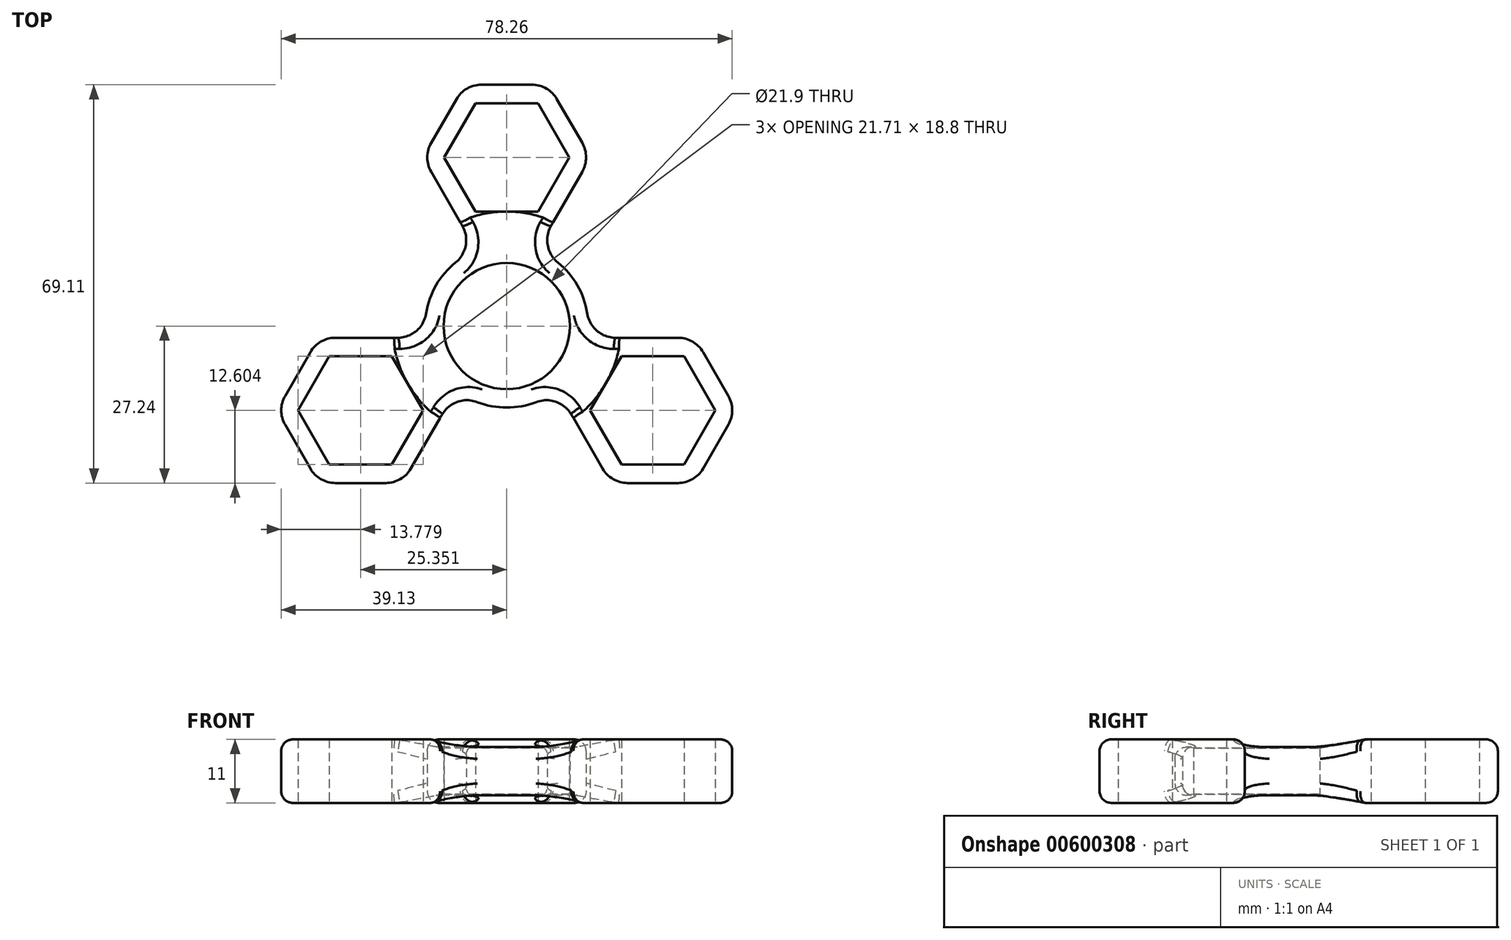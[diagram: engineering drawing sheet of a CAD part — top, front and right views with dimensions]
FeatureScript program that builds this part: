
annotation { "Feature Type Name" : "Feature", "Feature Type Description" : "" }
export const myFeature = defineFeature(function(context is Context, id is Id, definition is map)
    precondition{}
    {
        {
            var Q0;
            Q0=qCreatedBy(makeId("Top.planeOp"),FACE);
            var sketch = newSketch(context, id + "F0", { "sketchPlane" : qUnion([Q0])});
            skCircle(sketch, "E0", {"center": v(0, 0) * mm, "radius": 42.5 * mm, "construction": true});
            skLineSegment(sketch, "E1", {"start": v(0, 29.27) * mm, "end": v(0, 0) * mm, "construction": true});
            skLineSegment(sketch, "E2", {"start": v(0, 0) * mm, "end": v(-25.35, -14.64) * mm, "construction": true});
            skLineSegment(sketch, "E3", {"start": v(0, 0) * mm, "end": v(25.35, -14.64) * mm, "construction": true});
            skCircle(sketch, "E4.cCircle", {"center": v(0, 29.27) * mm, "radius": 9.4 * mm, "construction": true});
            skLineSegment(sketch, "E4.0", {"start": v(10.85, 29.27) * mm, "end": v(5.43, 19.87) * mm});
            skLineSegment(sketch, "E4.1", {"start": v(5.43, 19.87) * mm, "end": v(-5.43, 19.87) * mm});
            skLineSegment(sketch, "E4.2", {"start": v(-5.43, 19.87) * mm, "end": v(-10.85, 29.27) * mm});
            skLineSegment(sketch, "E4.3", {"start": v(-10.85, 29.27) * mm, "end": v(-5.43, 38.67) * mm});
            skLineSegment(sketch, "E4.4", {"start": v(-5.43, 38.67) * mm, "end": v(5.43, 38.67) * mm});
            skLineSegment(sketch, "E4.5", {"start": v(5.43, 38.67) * mm, "end": v(10.85, 29.27) * mm});
            skPoint(sketch, "E4.0.midPoint", {"position": v(8.14, 24.57) * mm});
            skCircle(sketch, "E5.cCircle", {"center": v(0, 29.27) * mm, "radius": 12.6 * mm, "construction": true});
            skLineSegment(sketch, "E5.0", {"start": v(14.55, 29.27) * mm, "end": v(7.27, 16.67) * mm});
            skLineSegment(sketch, "E5.1", {"start": v(7.27, 16.67) * mm, "end": v(0, 16.67) * mm});
            skLineSegment(sketch, "E5.2", {"start": v(-7.27, 16.67) * mm, "end": v(-14.55, 29.27) * mm});
            skLineSegment(sketch, "E5.3", {"start": v(-14.55, 29.27) * mm, "end": v(-7.27, 41.87) * mm});
            skLineSegment(sketch, "E5.4", {"start": v(-7.27, 41.87) * mm, "end": v(7.27, 41.87) * mm});
            skLineSegment(sketch, "E5.5", {"start": v(7.27, 41.87) * mm, "end": v(14.55, 29.27) * mm});
            skPoint(sketch, "E5.0.midPoint", {"position": v(10.91, 22.97) * mm});
            skLineSegment(sketch, "E6", {"start": v(-7.27, 16.67) * mm, "end": v(-5.24, 13.14) * mm});
            skLineSegment(sketch, "E7", {"start": v(7.27, 16.67) * mm, "end": v(5.24, 13.14) * mm});
            skCircle(sketch, "E8", {"center": v(0, 0) * mm, "radius": 10.95 * mm});
            skCircle(sketch, "E9.cCircle", {"center": v(25.35, -14.64) * mm, "radius": 9.4 * mm, "construction": true});
            skLineSegment(sketch, "E9.0", {"start": v(36.2, -14.64) * mm, "end": v(30.78, -24.04) * mm});
            skLineSegment(sketch, "E9.1", {"start": v(30.78, -24.04) * mm, "end": v(19.92, -24.04) * mm});
            skLineSegment(sketch, "E9.2", {"start": v(19.92, -24.04) * mm, "end": v(14.5, -14.64) * mm});
            skLineSegment(sketch, "E9.3", {"start": v(14.5, -14.64) * mm, "end": v(19.92, -5.24) * mm});
            skLineSegment(sketch, "E9.4", {"start": v(19.92, -5.24) * mm, "end": v(30.78, -5.24) * mm});
            skLineSegment(sketch, "E9.5", {"start": v(30.78, -5.24) * mm, "end": v(36.2, -14.64) * mm});
            skPoint(sketch, "E9.0.midPoint", {"position": v(33.5, -19.34) * mm});
            skCircle(sketch, "E10.cCircle", {"center": v(25.35, -14.64) * mm, "radius": 12.6 * mm, "construction": true});
            skLineSegment(sketch, "E10.0", {"start": v(39.9, -14.64) * mm, "end": v(32.63, -27.24) * mm});
            skLineSegment(sketch, "E10.1", {"start": v(32.63, -27.24) * mm, "end": v(18.08, -27.24) * mm});
            skLineSegment(sketch, "E10.2", {"start": v(18.08, -27.24) * mm, "end": v(10.8, -14.64) * mm});
            skLineSegment(sketch, "E10.3", {"start": v(10.8, -14.64) * mm, "end": v(14.44, -8.34) * mm});
            skLineSegment(sketch, "E10.4", {"start": v(18.08, -2.04) * mm, "end": v(32.63, -2.04) * mm});
            skLineSegment(sketch, "E10.5", {"start": v(32.63, -2.04) * mm, "end": v(39.9, -14.64) * mm});
            skPoint(sketch, "E10.0.midPoint", {"position": v(36.26, -20.94) * mm});
            skCircle(sketch, "E11.cCircle", {"center": v(-25.35, -14.64) * mm, "radius": 9.4 * mm, "construction": true});
            skLineSegment(sketch, "E11.0", {"start": v(-14.5, -14.64) * mm, "end": v(-19.92, -24.04) * mm});
            skLineSegment(sketch, "E11.1", {"start": v(-19.92, -24.04) * mm, "end": v(-30.78, -24.04) * mm});
            skLineSegment(sketch, "E11.2", {"start": v(-30.78, -24.04) * mm, "end": v(-36.2, -14.64) * mm});
            skLineSegment(sketch, "E11.3", {"start": v(-36.2, -14.64) * mm, "end": v(-30.78, -5.24) * mm});
            skLineSegment(sketch, "E11.4", {"start": v(-30.78, -5.24) * mm, "end": v(-19.92, -5.24) * mm});
            skLineSegment(sketch, "E11.5", {"start": v(-19.92, -5.24) * mm, "end": v(-14.5, -14.64) * mm});
            skPoint(sketch, "E11.0.midPoint", {"position": v(-17.21, -19.34) * mm});
            skCircle(sketch, "E12.cCircle", {"center": v(-25.35, -14.64) * mm, "radius": 12.6 * mm, "construction": true});
            skLineSegment(sketch, "E12.0", {"start": v(-10.8, -14.64) * mm, "end": v(-18.08, -27.24) * mm});
            skLineSegment(sketch, "E12.1", {"start": v(-18.08, -27.24) * mm, "end": v(-32.63, -27.24) * mm});
            skLineSegment(sketch, "E12.2", {"start": v(-32.63, -27.24) * mm, "end": v(-39.9, -14.64) * mm});
            skLineSegment(sketch, "E12.3", {"start": v(-39.9, -14.64) * mm, "end": v(-32.63, -2.04) * mm});
            skLineSegment(sketch, "E12.4", {"start": v(-32.63, -2.04) * mm, "end": v(-18.08, -2.04) * mm});
            skLineSegment(sketch, "E12.5", {"start": v(-18.08, -2.04) * mm, "end": v(-14.44, -8.34) * mm});
            skPoint(sketch, "E12.0.midPoint", {"position": v(-14.44, -20.94) * mm});
            skLineSegment(sketch, "E13", {"start": v(-18.08, -2.04) * mm, "end": v(-14, -2.04) * mm});
            skLineSegment(sketch, "E14", {"start": v(-10.8, -14.64) * mm, "end": v(-8.76, -11.1) * mm});
            skLineSegment(sketch, "E15", {"start": v(10.8, -14.64) * mm, "end": v(8.76, -11.1) * mm});
            skLineSegment(sketch, "E16", {"start": v(18.08, -2.04) * mm, "end": v(14, -2.04) * mm});
            skArc(sketch, "E17", {"start": v(-5.24, 13.14) * mm, "mid": v(-12.25, 7.08) * mm, "end": v(-14, -2.04) * mm});
            skArc(sketch, "E18.trimOffspring", {"start": v(-8.76, -11.1) * mm, "mid": v(0, -14.15) * mm, "end": v(8.76, -11.1) * mm});
            skArc(sketch, "E19.trimOffspring", {"start": v(14, -2.04) * mm, "mid": v(12.25, 7.07) * mm, "end": v(5.24, 13.14) * mm});
            skSolve(sketch);
        }
        {
            var Q0;
            Q0=qSketchRegion(id+"F0",true);
            extrude(context, id + "F1", {"entities" : qUnion([Q0]), "endBound" : BoundingType.SYMMETRIC, "depth" : 11 * mm, "offsetDistance" : 25 * mm});
        }
        {
            var Q0;
            Q0=qCreatedBy(makeId("Right.planeOp"),FACE);
            var sketch = newSketch(context, id + "F2", { "sketchPlane" : qUnion([Q0])});
            skLineSegment(sketch, "E20", {"start": v(-10.95, -5.5) * mm, "end": v(-10.95, 5.5) * mm, "construction": true});
            skLineSegment(sketch, "E21", {"start": v(10.95, 5.5) * mm, "end": v(10.95, -5.5) * mm, "construction": true});
            skLineSegment(sketch, "E22.0.0", {"start": v(19.87, -5.5) * mm, "end": v(29.27, -5.5) * mm, "construction": true});
            skLineSegment(sketch, "E22.0.1", {"start": v(29.27, -5.5) * mm, "end": v(29.27, 5.5) * mm, "construction": true});
            skLineSegment(sketch, "E22.0.2", {"start": v(29.27, 5.5) * mm, "end": v(19.87, 5.5) * mm, "construction": true});
            skLineSegment(sketch, "E22.0.3", {"start": v(19.87, 5.5) * mm, "end": v(19.87, -5.5) * mm, "construction": true});
            skLineSegment(sketch, "E23", {"start": v(10.95, 4) * mm, "end": v(19.87, 5.5) * mm});
            skLineSegment(sketch, "E24", {"start": v(19.87, 5.5) * mm, "end": v(10.95, 5.5) * mm});
            skLineSegment(sketch, "E25", {"start": v(10.95, 5.5) * mm, "end": v(10.95, 4) * mm});
            skLineSegment(sketch, "E26", {"start": v(10.95, -4) * mm, "end": v(10.95, -5.5) * mm});
            skLineSegment(sketch, "E27", {"start": v(10.95, -5.5) * mm, "end": v(19.87, -5.5) * mm});
            skLineSegment(sketch, "E28", {"start": v(19.87, -5.5) * mm, "end": v(10.95, -4) * mm});
            skLineSegment(sketch, "E29", {"start": v(0, 0) * mm, "end": v(0, 13.53) * mm, "construction": true});
            skSolve(sketch);
        }
        {
            var Q0;
            Q0=qSketchRegion(id+"F2",true);
            var Q1;
            Q1=sQuery(id+"F2.wireOp",EDGE,"E29");
            revolve(context, id + "F3", {"operationType" : NewBodyOperationType.REMOVE, "surfaceOperationType" : NewSurfaceOperationType.NEW, "entities" : qUnion([Q0]), "axis" : qUnion([Q1]), "revolveType" : RevolveType.FULL, "oppositeDirection" : true});
        }
        {
            var Q0;
            Q0=makeQuery(id+"F1.opExtrude","SWEPT_EDGE",EDGE,{"disambiguationData":[OSD([sQuery(id+"F0.wireOp",EDGE,"O4FCEVp2-a76e-EbQX-IVHh-MGuyo65jWMq8"),sQuery(id+"F0.wireOp",EDGE,"E6")])]});
            var Q1;
            Q1=makeQuery(id+"F1.opExtrude","SWEPT_EDGE",EDGE,{"disambiguationData":[OSD([sQuery(id+"F0.wireOp",EDGE,"O4FCEVp2-a76e-EbQX-IVHh-MGuyo65jWMq8"),sQuery(id+"F0.wireOp",EDGE,"E13")])]});
            var Q2;
            Q2=makeQuery(id+"F1.opExtrude","SWEPT_EDGE",EDGE,{"disambiguationData":[OSD([sQuery(id+"F0.wireOp",EDGE,"O4FCEVp2-a76e-EbQX-IVHh-MGuyo65jWMq8"),sQuery(id+"F0.wireOp",EDGE,"E15")])]});
            var Q3;
            Q3=makeQuery(id+"F1.opExtrude","SWEPT_EDGE",EDGE,{"disambiguationData":[OSD([sQuery(id+"F0.wireOp",EDGE,"O4FCEVp2-a76e-EbQX-IVHh-MGuyo65jWMq8"),sQuery(id+"F0.wireOp",EDGE,"E14")])]});
            var Q4;
            Q4=makeQuery(id+"F1.opExtrude","SWEPT_EDGE",EDGE,{"disambiguationData":[OSD([sQuery(id+"F0.wireOp",EDGE,"O4FCEVp2-a76e-EbQX-IVHh-MGuyo65jWMq8"),sQuery(id+"F0.wireOp",EDGE,"E16")])]});
            var Q5;
            Q5=makeQuery(id+"F1.opExtrude","SWEPT_EDGE",EDGE,{"disambiguationData":[OSD([sQuery(id+"F0.wireOp",EDGE,"O4FCEVp2-a76e-EbQX-IVHh-MGuyo65jWMq8"),sQuery(id+"F0.wireOp",EDGE,"E7")])]});
            var Q6;
            Q6=makeQuery(id+"F1.opExtrude","SWEPT_EDGE",EDGE,{"disambiguationData":[OSD([sQuery(id+"F0.wireOp",EDGE,"E10.4"),sQuery(id+"F0.wireOp",EDGE,"E10.5")])]});
            var Q7;
            Q7=makeQuery(id+"F1.opExtrude","SWEPT_EDGE",EDGE,{"disambiguationData":[OSD([sQuery(id+"F0.wireOp",EDGE,"E10.0"),sQuery(id+"F0.wireOp",EDGE,"E10.5")])]});
            var Q8;
            Q8=makeQuery(id+"F1.opExtrude","SWEPT_EDGE",EDGE,{"disambiguationData":[OSD([sQuery(id+"F0.wireOp",EDGE,"E10.0"),sQuery(id+"F0.wireOp",EDGE,"E10.1")])]});
            var Q9;
            Q9=makeQuery(id+"F1.opExtrude","SWEPT_EDGE",EDGE,{"disambiguationData":[OSD([sQuery(id+"F0.wireOp",EDGE,"E10.1"),sQuery(id+"F0.wireOp",EDGE,"E10.2")])]});
            var Q10;
            Q10=makeQuery(id+"F1.opExtrude","SWEPT_EDGE",EDGE,{"disambiguationData":[OSD([sQuery(id+"F0.wireOp",EDGE,"E12.0"),sQuery(id+"F0.wireOp",EDGE,"E12.1")])]});
            var Q11;
            Q11=makeQuery(id+"F1.opExtrude","SWEPT_EDGE",EDGE,{"disambiguationData":[OSD([sQuery(id+"F0.wireOp",EDGE,"E12.1"),sQuery(id+"F0.wireOp",EDGE,"E12.2")])]});
            var Q12;
            Q12=makeQuery(id+"F1.opExtrude","SWEPT_EDGE",EDGE,{"disambiguationData":[OSD([sQuery(id+"F0.wireOp",EDGE,"E12.2"),sQuery(id+"F0.wireOp",EDGE,"E12.3")])]});
            var Q13;
            Q13=makeQuery(id+"F1.opExtrude","SWEPT_EDGE",EDGE,{"disambiguationData":[OSD([sQuery(id+"F0.wireOp",EDGE,"E12.3"),sQuery(id+"F0.wireOp",EDGE,"E12.4")])]});
            var Q14;
            Q14=makeQuery(id+"F1.opExtrude","SWEPT_EDGE",EDGE,{"disambiguationData":[OSD([sQuery(id+"F0.wireOp",EDGE,"E5.2"),sQuery(id+"F0.wireOp",EDGE,"E5.3")])]});
            var Q15;
            Q15=makeQuery(id+"F1.opExtrude","SWEPT_EDGE",EDGE,{"disambiguationData":[OSD([sQuery(id+"F0.wireOp",EDGE,"E5.3"),sQuery(id+"F0.wireOp",EDGE,"E5.4")])]});
            var Q16;
            Q16=makeQuery(id+"F1.opExtrude","SWEPT_EDGE",EDGE,{"disambiguationData":[OSD([sQuery(id+"F0.wireOp",EDGE,"E5.4"),sQuery(id+"F0.wireOp",EDGE,"E5.5")])]});
            var Q17;
            Q17=makeQuery(id+"F1.opExtrude","SWEPT_EDGE",EDGE,{"disambiguationData":[OSD([sQuery(id+"F0.wireOp",EDGE,"E5.0"),sQuery(id+"F0.wireOp",EDGE,"E5.5")])]});
            fillet(context, id + "F4", {"entities" : qUnion([Q0, Q1, Q2, Q3, Q4, Q5, Q6, Q7, Q8, Q9, Q10, Q11, Q12, Q13, Q14, Q15, Q16, Q17]), "radius" : 5 * mm, "tangentPropagation" : true, "allowEdgeOverflow" : false});
        }
        {
            var Q0;
            Q0=makeQuery(id+"F1.opExtrude","CAP_EDGE",EDGE,{"disambiguationData":[OSD([sQuery(id+"F0.wireOp",EDGE,"E12.1")])],"isStart":false});
            var Q1;
            Q1=makeQuery(id+"F1.opExtrude","CAP_EDGE",EDGE,{"disambiguationData":[OSD([sQuery(id+"F0.wireOp",EDGE,"E12.1")])],"isStart":true});
            var Q2;
            Q2=makeQuery(id+"F3.boolean.opBoolean","INTERSECT",EDGE,{"derivedFrom":[makeQuery(id+"F1.opExtrude","SWEPT_FACE",FACE,{"disambiguationData":[OSD([sQuery(id+"F0.wireOp",EDGE,"E17")])]}),makeQuery(id+"F3.opRevolve","SWEPT_FACE",FACE,{"disambiguationData":[OSD([sQuery(id+"F2.wireOp",EDGE,"E23")])]})]});
            var Q3;
            Q3=makeQuery(id+"F1.opExtrude","CAP_EDGE",EDGE,{"disambiguationData":[OSD([sQuery(id+"F0.wireOp",EDGE,"E5.3")])],"isStart":false});
            var Q4;
            Q4=makeQuery(id+"F3.boolean.opBoolean","INTERSECT",EDGE,{"derivedFrom":[makeQuery(id+"F1.opExtrude","SWEPT_FACE",FACE,{"disambiguationData":[OSD([sQuery(id+"F0.wireOp",EDGE,"E19.trimOffspring")])]}),makeQuery(id+"F3.opRevolve","SWEPT_FACE",FACE,{"disambiguationData":[OSD([sQuery(id+"F2.wireOp",EDGE,"E23")])]})]});
            var Q5;
            Q5=makeQuery(id+"F1.opExtrude","CAP_EDGE",EDGE,{"disambiguationData":[OSD([sQuery(id+"F0.wireOp",EDGE,"E10.0")])],"isStart":false});
            var Q6;
            Q6=makeQuery(id+"F3.boolean.opBoolean","INTERSECT",EDGE,{"derivedFrom":[makeQuery(id+"F1.opExtrude","SWEPT_FACE",FACE,{"disambiguationData":[OSD([sQuery(id+"F0.wireOp",EDGE,"E18.trimOffspring")])]}),makeQuery(id+"F3.opRevolve","SWEPT_FACE",FACE,{"disambiguationData":[OSD([sQuery(id+"F2.wireOp",EDGE,"E23")])]})]});
            var Q7;
            Q7=makeQuery(id+"F3.boolean.opBoolean","INTERSECT",EDGE,{"derivedFrom":[makeQuery(id+"F1.opExtrude","SWEPT_FACE",FACE,{"disambiguationData":[OSD([sQuery(id+"F0.wireOp",EDGE,"E18.trimOffspring")])]}),makeQuery(id+"F3.opRevolve","SWEPT_FACE",FACE,{"disambiguationData":[OSD([sQuery(id+"F2.wireOp",EDGE,"E28")])]})]});
            var Q8;
            Q8=makeQuery(id+"F1.opExtrude","CAP_EDGE",EDGE,{"disambiguationData":[OSD([sQuery(id+"F0.wireOp",EDGE,"E10.0")])],"isStart":true});
            var Q9;
            Q9=makeQuery(id+"F1.opExtrude","CAP_EDGE",EDGE,{"disambiguationData":[OSD([sQuery(id+"F0.wireOp",EDGE,"E5.4")])],"isStart":true});
            var Q10;
            Q10=makeQuery(id+"F3.boolean.opBoolean","INTERSECT",EDGE,{"derivedFrom":[makeQuery(id+"F1.opExtrude","SWEPT_FACE",FACE,{"disambiguationData":[OSD([sQuery(id+"F0.wireOp",EDGE,"E19.trimOffspring")])]}),makeQuery(id+"F3.opRevolve","SWEPT_FACE",FACE,{"disambiguationData":[OSD([sQuery(id+"F2.wireOp",EDGE,"E28")])]})]});
            var Q11;
            Q11=makeQuery(id+"F3.boolean.opBoolean","INTERSECT",EDGE,{"derivedFrom":[makeQuery(id+"F1.opExtrude","SWEPT_FACE",FACE,{"disambiguationData":[OSD([sQuery(id+"F0.wireOp",EDGE,"E17")])]}),makeQuery(id+"F3.opRevolve","SWEPT_FACE",FACE,{"disambiguationData":[OSD([sQuery(id+"F2.wireOp",EDGE,"E28")])]})]});
            fillet(context, id + "F5", {"entities" : qUnion([Q0, Q1, Q2, Q3, Q4, Q5, Q6, Q7, Q8, Q9, Q10, Q11]), "radius" : 2 * mm, "tangentPropagation" : true, "allowEdgeOverflow" : false});
        }
    });
